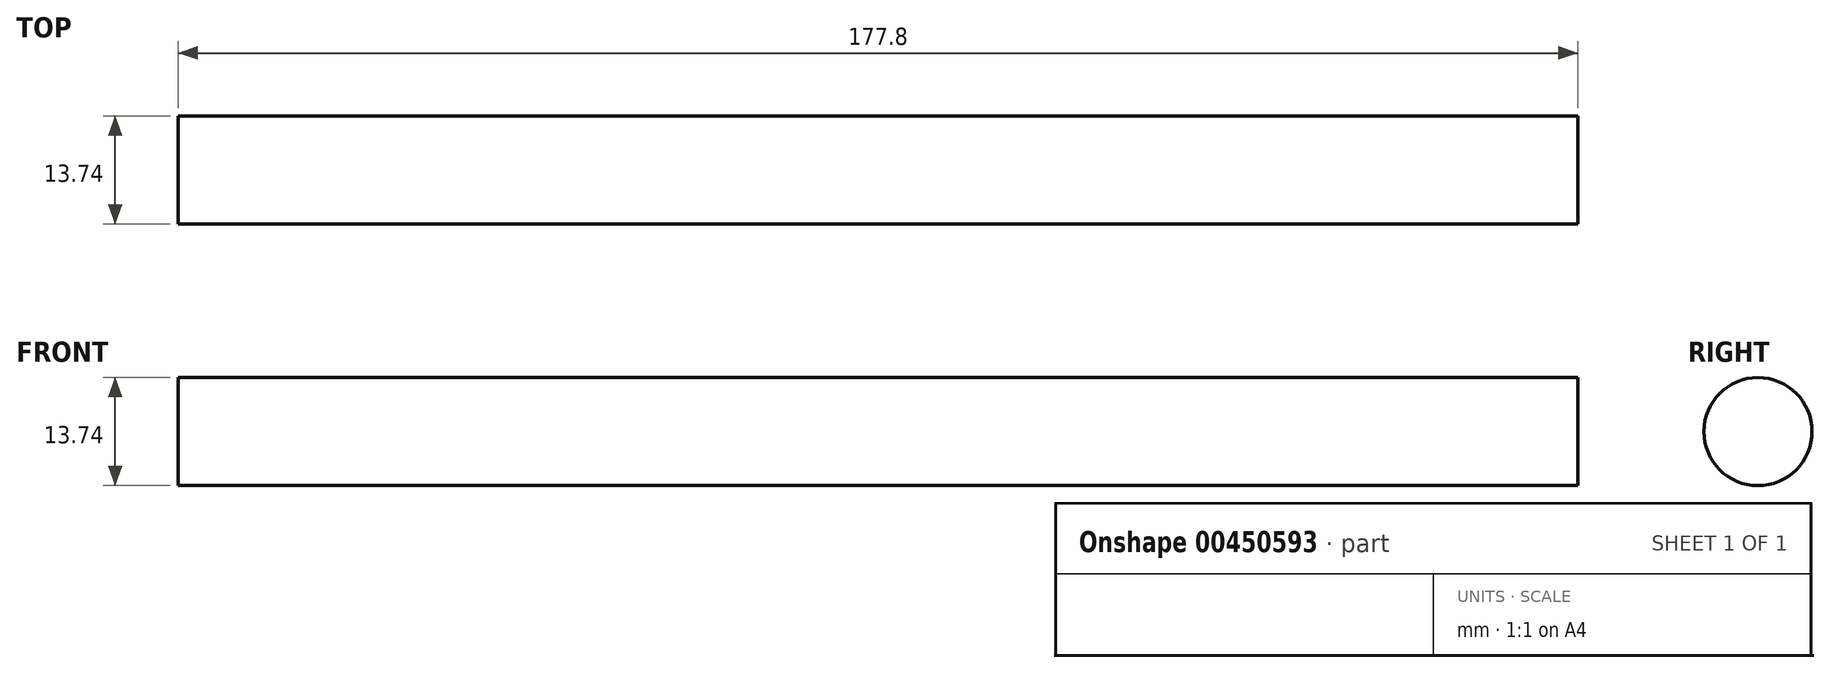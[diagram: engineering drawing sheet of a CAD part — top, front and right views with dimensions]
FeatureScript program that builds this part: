
annotation { "Feature Type Name" : "Feature", "Feature Type Description" : "" }
export const myFeature = defineFeature(function(context is Context, id is Id, definition is map)
    precondition{}
    {
        {
            var Q0;
            Q0=qCreatedBy(makeId("Right.planeOp"),FACE);
            var sketch = newSketch(context, id + "F0", { "sketchPlane" : qUnion([Q0])});
            skCircle(sketch, "E0", {"center": v(0, 0) * mm, "radius": 6.87 * mm});
            skSolve(sketch);
        }
        {
            var Q0;
            Q0=makeQuery(id+"F0.imprint","IMPRINT",FACE,{"disambiguationData":[TD([[makeQuery(id+"F0.imprint","IMPRINT",EDGE,{"derivedFrom":sQuery(id+"F0.wireOp",EDGE,"E0")}),1.0]])]});
            extrude(context, id + "F1", {"entities" : qUnion([Q0]), "depth" : 177.8 * mm});
        }
    });
